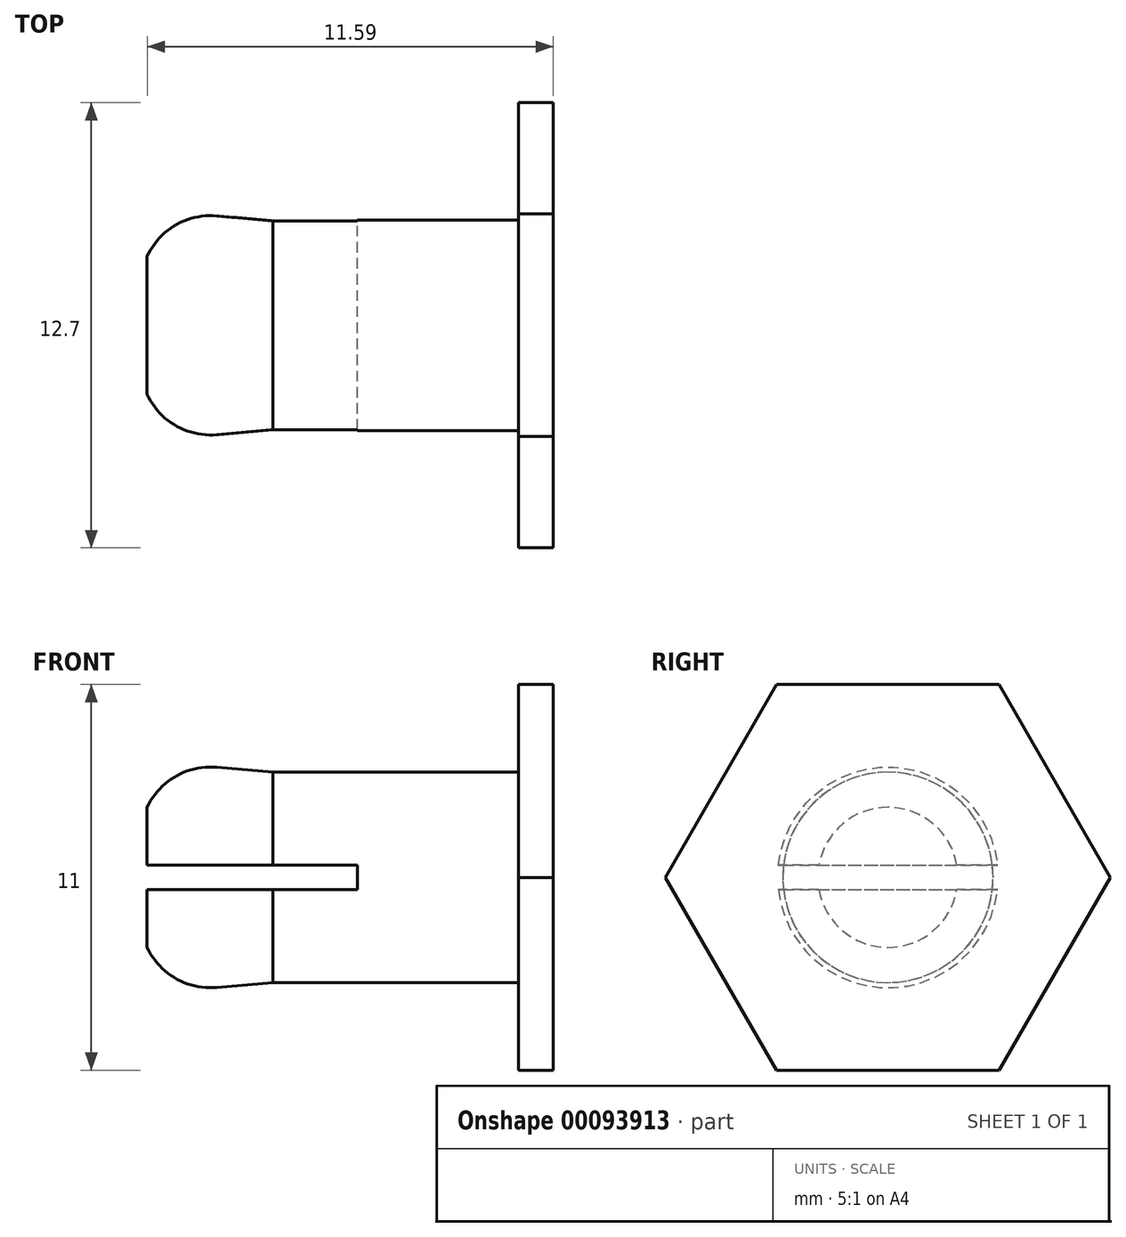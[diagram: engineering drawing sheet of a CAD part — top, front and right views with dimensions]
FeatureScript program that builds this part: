
annotation { "Feature Type Name" : "Feature", "Feature Type Description" : "" }
export const myFeature = defineFeature(function(context is Context, id is Id, definition is map)
    precondition{}
    {
        {
            var Q0;
            Q0=qCreatedBy(makeId("Front.planeOp"),FACE);
            var sketch = newSketch(context, id + "F0", { "sketchPlane" : qUnion([Q0])});
            skLineSegment(sketch, "E0", {"start": v(0, 0) * mm, "end": v(0, 6) * mm});
            skLineSegment(sketch, "E1", {"start": v(0, 6) * mm, "end": v(-1, 6) * mm});
            skLineSegment(sketch, "E2", {"start": v(-1, 6) * mm, "end": v(-1, 3) * mm});
            skLineSegment(sketch, "E3", {"start": v(-1, 3) * mm, "end": v(-8, 3) * mm});
            skLineSegment(sketch, "E4", {"start": v(-8, 3) * mm, "end": v(-9.61, 3.14) * mm});
            skLineSegment(sketch, "E5", {"start": v(-11.6, 2) * mm, "end": v(-11.6, 2) * mm});
            skLineSegment(sketch, "E6", {"start": v(-11.6, 2) * mm, "end": v(-11.6, 0) * mm});
            skLineSegment(sketch, "E7", {"start": v(-11.6, 0) * mm, "end": v(0, 0) * mm});
            skPoint(sketch, "E8.visualSharp", {"position": v(-11, 3.26) * mm});
            skArc(sketch, "E8.filletArc", {"start": v(-9.61, 3.14) * mm, "mid": v(-10.78, 2.88) * mm, "end": v(-11.6, 2) * mm});
            skSolve(sketch);
        }
        {
            var Q0;
            Q0=makeQuery(id+"F0.imprint","IMPRINT",FACE,{"disambiguationData":[TD([[makeQuery(id+"F0.imprint","IMPRINT",EDGE,{"derivedFrom":sQuery(id+"F0.wireOp",EDGE,"E0")}),1.0]])]});
            var Q1;
            Q1=sQuery(id+"F0.wireOp",EDGE,"E7");
            revolve(context, id + "F1", {"entities" : qUnion([Q0]), "axis" : qUnion([Q1]), "revolveType" : RevolveType.FULL});
        }
        {
            var Q0;
            Q0=makeQuery(id+"F1.opRevolve","SWEPT_FACE",FACE,{"disambiguationData":[OSD([sQuery(id+"F0.wireOp",EDGE,"E6")])]});
            var sketch = newSketch(context, id + "F2", { "sketchPlane" : qUnion([Q0])});
            skLineSegment(sketch, "E9.bottom", {"start": v(4, 0.35) * mm, "end": v(-4, 0.35) * mm});
            skLineSegment(sketch, "E9.top", {"start": v(4, -0.35) * mm, "end": v(-4, -0.35) * mm});
            skLineSegment(sketch, "E9.left", {"start": v(4, 0.35) * mm, "end": v(4, -0.35) * mm});
            skLineSegment(sketch, "E9.right", {"start": v(-4, 0.35) * mm, "end": v(-4, -0.35) * mm});
            skPoint(sketch, "E9.middle", {"position": v(0, 0) * mm});
            skLineSegment(sketch, "E10.bottom", {"start": v(-4, 0.35) * mm, "end": v(4, 0.35) * mm});
            skLineSegment(sketch, "E10.top", {"start": v(-4, -4.18) * mm, "end": v(4, -4.18) * mm});
            skLineSegment(sketch, "E10.left", {"start": v(-4, 0.35) * mm, "end": v(-4, -4.18) * mm});
            skLineSegment(sketch, "E10.right", {"start": v(4, 0.35) * mm, "end": v(4, -4.18) * mm});
            skArc(sketch, "E11", {"start": v(-2.98, -0.35) * mm, "mid": v(0, -3) * mm, "end": v(2.98, -0.35) * mm});
            skLineSegment(sketch, "E12", {"start": v(-0.25, 0.35) * mm, "end": v(-0.25, 4.35) * mm});
            skLineSegment(sketch, "E13", {"start": v(-0.25, 4.35) * mm, "end": v(0.25, 4.35) * mm});
            skLineSegment(sketch, "E14", {"start": v(0.25, 4.35) * mm, "end": v(0.25, 0.35) * mm});
            skPoint(sketch, "E15", {"position": v(0, 4.35) * mm});
            skLineSegment(sketch, "E16", {"start": v(-0.25, 0.35) * mm, "end": v(-0.25, 0) * mm});
            skLineSegment(sketch, "E17", {"start": v(0.25, 0) * mm, "end": v(0.25, 0.35) * mm});
            skLineSegment(sketch, "E18", {"start": v(-0.25, 0) * mm, "end": v(-0.25, -0.35) * mm});
            skLineSegment(sketch, "E19", {"start": v(0.25, 0) * mm, "end": v(0.25, -0.35) * mm});
            skSolve(sketch);
        }
        {
            var Q0;
            {var subQ0=sQuery(id+"F2.wireOp",EDGE,"E10.left");var subQ1=sQuery(id+"F2.wireOp",EDGE,"E9.top");var subQ2=makeQuery(id+"F2.imprint","INTERSECT",VERTEX,{"derivedFrom":[subQ1,subQ0]});Q0=makeQuery(id+"F2.imprint","IMPRINT",FACE,{"disambiguationData":[TD([[makeQuery(id+"F2.imprint","IMPRINT",EDGE,{"disambiguationData":[TD([[subQ2,1.0]])],"derivedFrom":subQ1}),-1.0]])]});}
            var Q1;
            {var subQ0=sQuery(id+"F2.wireOp",EDGE,"E9.top");var subQ1=sQuery(id+"F0.wireOp",EDGE,"E6");var subQ2=makeQuery(id+"F1.opRevolve","SWEPT_EDGE",EDGE,{"disambiguationData":[OSD([subQ1,sQuery(id+"F0.wireOp",EDGE,"7DEYfaqh-BLmM-Zio8-RinN-fUETocERDkPJ")])]});var subQ3=makeQuery(id+"F2.imprint","INTERSECT",VERTEX,{"disambiguationData":[OD(1.0)],"derivedFrom":[subQ2,subQ0]});Q1=makeQuery(id+"F2.imprint","IMPRINT",FACE,{"disambiguationData":[TD([[makeQuery(id+"F2.imprint","IMPRINT",EDGE,{"disambiguationData":[TD([[subQ3,-1.0]])],"derivedFrom":subQ0}),-1.0]])]});}
            var Q2;
            {var subQ1=sQuery(id+"F2.wireOp",EDGE,"E16");Q2=makeQuery(id+"F2.imprint","IMPRINT",FACE,{"disambiguationData":[TD([[makeQuery(id+"F2.imprint","IMPRINT",EDGE,{"derivedFrom":subQ1}),-1.0]])]});}
            var Q3;
            {var subQ0=sQuery(id+"F2.wireOp",EDGE,"E16");Q3=makeQuery(id+"F2.imprint","IMPRINT",FACE,{"disambiguationData":[TD([[makeQuery(id+"F2.imprint","IMPRINT",EDGE,{"derivedFrom":subQ0}),1.0]])]});}
            var Q4;
            {var subQ0=sQuery(id+"F2.wireOp",EDGE,"E10.right");var subQ1=sQuery(id+"F2.wireOp",EDGE,"E9.top");var subQ2=makeQuery(id+"F2.imprint","INTERSECT",VERTEX,{"derivedFrom":[subQ1,subQ0]});Q4=makeQuery(id+"F2.imprint","IMPRINT",FACE,{"disambiguationData":[TD([[makeQuery(id+"F2.imprint","IMPRINT",EDGE,{"disambiguationData":[TD([[subQ2,-1.0]])],"derivedFrom":subQ1}),-1.0]])]});}
            var Q5;
            {var subQ0=sQuery(id+"F2.wireOp",EDGE,"E9.top");var subQ1=sQuery(id+"F0.wireOp",EDGE,"E6");var subQ2=makeQuery(id+"F1.opRevolve","SWEPT_EDGE",EDGE,{"disambiguationData":[OSD([sQuery(id+"F0.wireOp",EDGE,"E5"),subQ1])]});var subQ3=makeQuery(id+"F2.imprint","INTERSECT",VERTEX,{"disambiguationData":[OD(0.0)],"derivedFrom":[subQ2,subQ0]});Q5=makeQuery(id+"F2.imprint","IMPRINT",FACE,{"disambiguationData":[TD([[makeQuery(id+"F2.imprint","IMPRINT",EDGE,{"disambiguationData":[TD([[subQ3,-1.0]])],"derivedFrom":subQ0}),-1.0]])]});}
            var Q6;
            {var subQ0=sQuery(id+"F2.wireOp",EDGE,"E17");Q6=makeQuery(id+"F2.imprint","IMPRINT",FACE,{"disambiguationData":[TD([[makeQuery(id+"F2.imprint","IMPRINT",EDGE,{"derivedFrom":subQ0}),-1.0]])]});}
            extrude(context, id + "F3", {"entities" : qUnion([Q0, Q1, Q2, Q3, Q4, Q5, Q6]), "operationType" : NewBodyOperationType.REMOVE, "oppositeDirection" : true, "depth" : 6 * mm});
        }
        {
            var Q0;
            Q0=makeQuery(id+"F1.opRevolve","SWEPT_FACE",FACE,{"disambiguationData":[OSD([sQuery(id+"F0.wireOp",EDGE,"E2")])]});
            var sketch = newSketch(context, id + "F4", { "sketchPlane" : qUnion([Q0])});
            skCircle(sketch, "E20.cCircle", {"center": v(0, 0) * mm, "radius": 5.5 * mm, "construction": true});
            skLineSegment(sketch, "E20.0", {"start": v(-3.18, 5.5) * mm, "end": v(3.18, 5.5) * mm});
            skLineSegment(sketch, "E20.1", {"start": v(3.18, 5.5) * mm, "end": v(6.35, 0) * mm});
            skLineSegment(sketch, "E20.2", {"start": v(6.35, 0) * mm, "end": v(3.18, -5.5) * mm});
            skLineSegment(sketch, "E20.3", {"start": v(3.18, -5.5) * mm, "end": v(-3.18, -5.5) * mm});
            skLineSegment(sketch, "E20.4", {"start": v(-3.18, -5.5) * mm, "end": v(-6.35, 0) * mm});
            skLineSegment(sketch, "E20.5", {"start": v(-6.35, 0) * mm, "end": v(-3.18, 5.5) * mm});
            skPoint(sketch, "E20.0.midPoint", {"position": v(0, 5.5) * mm});
            skLineSegment(sketch, "E21.bottom", {"start": v(-6.85, 6.5) * mm, "end": v(6.85, 6.5) * mm});
            skLineSegment(sketch, "E21.top", {"start": v(-6.85, -6.5) * mm, "end": v(6.85, -6.5) * mm});
            skLineSegment(sketch, "E21.left", {"start": v(-6.85, 6.5) * mm, "end": v(-6.85, -6.5) * mm});
            skLineSegment(sketch, "E21.right", {"start": v(6.85, 6.5) * mm, "end": v(6.85, -6.5) * mm});
            skSolve(sketch);
        }
        {
            var Q0;
            Q0 = qSketchRegion(id + "F4", true);
            var Q1;
            {var subQ1=sQuery(id+"F0.wireOp",EDGE,"E2");Q1=makeQuery(id+"F4.imprint","IMPRINT",FACE,{"disambiguationData":[TD([[makeQuery(id+"F4.imprint","IMPRINT",EDGE,{"derivedFrom":makeQuery(id+"F1.opRevolve","SWEPT_EDGE",EDGE,{"disambiguationData":[OSD([subQ1,sQuery(id+"F0.wireOp",EDGE,"E3")])]})}),-1.0]])]});}
            extrude(context, id + "F5", {"entities" : qUnion([Q0, Q1]), "operationType" : NewBodyOperationType.REMOVE, "oppositeDirection" : true, "depth" : 25 * mm});
        }
        {
            var Q0;
            {var subQ1=sQuery(id+"F0.wireOp",EDGE,"E2");Q0=makeQuery(id+"F4.imprint","IMPRINT",FACE,{"disambiguationData":[TD([[makeQuery(id+"F4.imprint","IMPRINT",EDGE,{"derivedFrom":makeQuery(id+"F1.opRevolve","SWEPT_EDGE",EDGE,{"disambiguationData":[OSD([subQ1,sQuery(id+"F0.wireOp",EDGE,"E3")])]})}),-1.0]])]});}
            var Q1;
            {var subQ0=sQuery(id+"F4.wireOp",EDGE,"E20.5");var subQ1=sQuery(id+"F4.wireOp",EDGE,"E20.0");var subQ2=makeQuery(id+"F4.imprint","INTERSECT",VERTEX,{"derivedFrom":[subQ1,subQ0]});Q1=makeQuery(id+"F4.imprint","IMPRINT",FACE,{"disambiguationData":[TD([[makeQuery(id+"F4.imprint","IMPRINT",EDGE,{"disambiguationData":[TD([[subQ2,-1.0]])],"derivedFrom":subQ1}),-1.0]])]});}
            var Q2;
            {var subQ0=sQuery(id+"F4.wireOp",EDGE,"E20.1");var subQ1=sQuery(id+"F4.wireOp",EDGE,"E20.0");var subQ2=makeQuery(id+"F4.imprint","INTERSECT",VERTEX,{"derivedFrom":[subQ1,subQ0]});Q2=makeQuery(id+"F4.imprint","IMPRINT",FACE,{"disambiguationData":[TD([[makeQuery(id+"F4.imprint","IMPRINT",EDGE,{"disambiguationData":[TD([[subQ2,1.0]])],"derivedFrom":subQ1}),-1.0]])]});}
            var Q3;
            {var subQ0=sQuery(id+"F4.wireOp",EDGE,"E20.2");var subQ1=sQuery(id+"F4.wireOp",EDGE,"E20.1");var subQ2=makeQuery(id+"F4.imprint","INTERSECT",VERTEX,{"derivedFrom":[subQ1,subQ0]});Q3=makeQuery(id+"F4.imprint","IMPRINT",FACE,{"disambiguationData":[TD([[makeQuery(id+"F4.imprint","IMPRINT",EDGE,{"disambiguationData":[TD([[subQ2,1.0]])],"derivedFrom":subQ1}),-1.0]])]});}
            var Q4;
            {var subQ0=sQuery(id+"F4.wireOp",EDGE,"E20.3");var subQ1=sQuery(id+"F4.wireOp",EDGE,"E20.2");var subQ2=makeQuery(id+"F4.imprint","INTERSECT",VERTEX,{"derivedFrom":[subQ1,subQ0]});Q4=makeQuery(id+"F4.imprint","IMPRINT",FACE,{"disambiguationData":[TD([[makeQuery(id+"F4.imprint","IMPRINT",EDGE,{"disambiguationData":[TD([[subQ2,1.0]])],"derivedFrom":subQ1}),-1.0]])]});}
            var Q5;
            {var subQ0=sQuery(id+"F4.wireOp",EDGE,"E20.4");var subQ1=sQuery(id+"F4.wireOp",EDGE,"E20.3");var subQ2=makeQuery(id+"F4.imprint","INTERSECT",VERTEX,{"derivedFrom":[subQ1,subQ0]});Q5=makeQuery(id+"F4.imprint","IMPRINT",FACE,{"disambiguationData":[TD([[makeQuery(id+"F4.imprint","IMPRINT",EDGE,{"disambiguationData":[TD([[subQ2,1.0]])],"derivedFrom":subQ1}),-1.0]])]});}
            var Q6;
            {var subQ0=sQuery(id+"F4.wireOp",EDGE,"E20.5");var subQ1=sQuery(id+"F4.wireOp",EDGE,"E20.4");var subQ2=makeQuery(id+"F4.imprint","INTERSECT",VERTEX,{"derivedFrom":[subQ1,subQ0]});Q6=makeQuery(id+"F4.imprint","IMPRINT",FACE,{"disambiguationData":[TD([[makeQuery(id+"F4.imprint","IMPRINT",EDGE,{"disambiguationData":[TD([[subQ2,1.0]])],"derivedFrom":subQ1}),-1.0]])]});}
            extrude(context, id + "F6", {"entities" : qUnion([Q0, Q1, Q2, Q3, Q4, Q5, Q6]), "operationType" : NewBodyOperationType.ADD, "oppositeDirection" : true, "depth" : 1 * mm});
        }
    });
